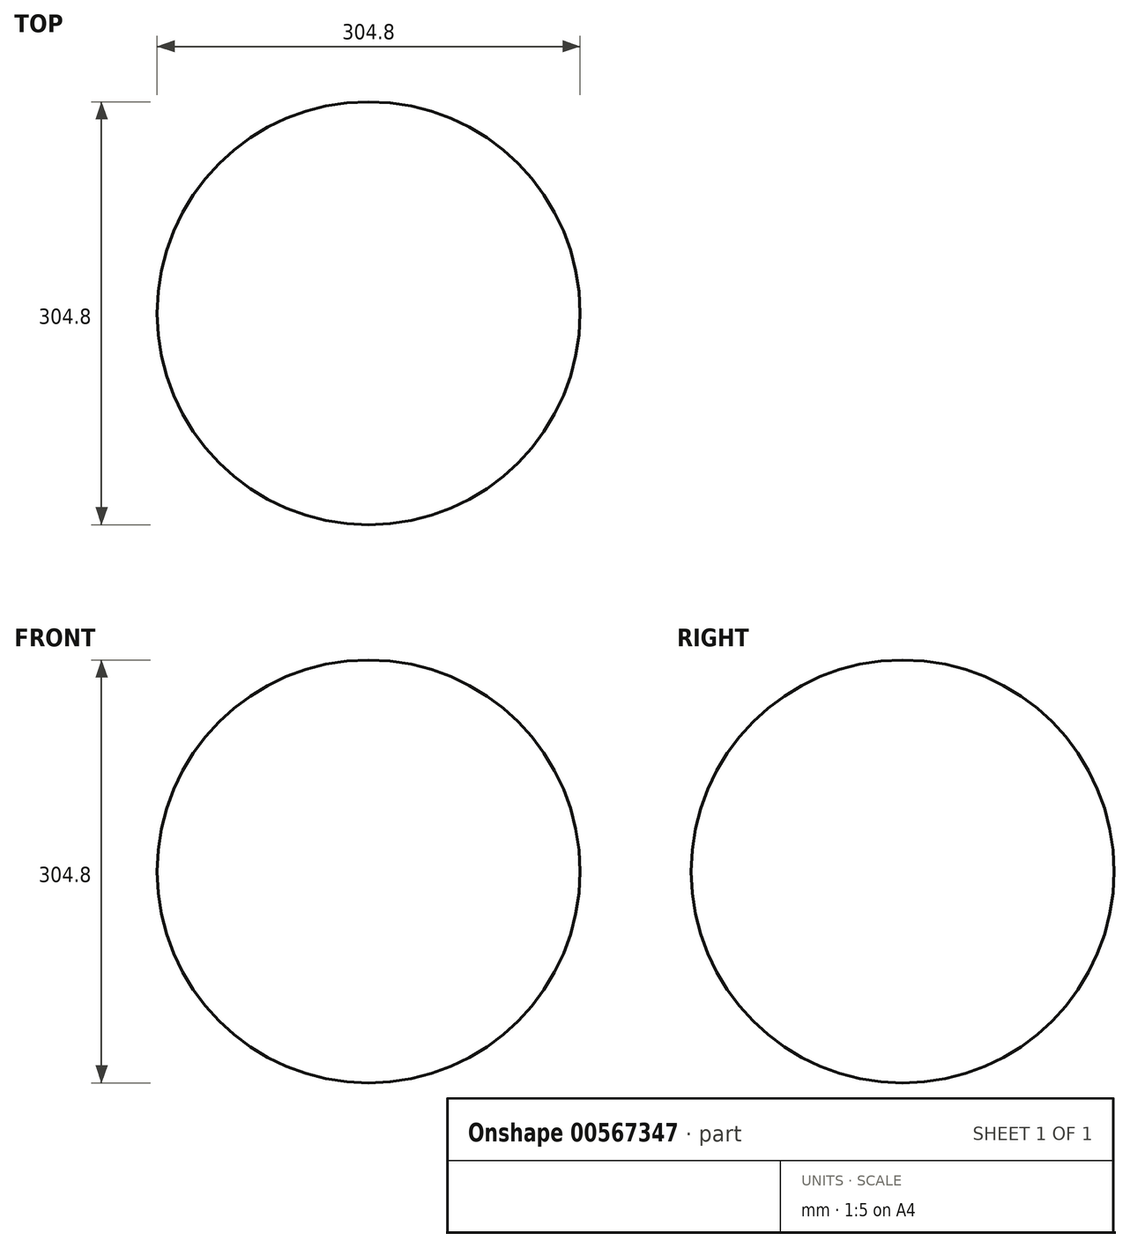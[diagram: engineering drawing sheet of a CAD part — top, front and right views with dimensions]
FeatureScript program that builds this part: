
annotation { "Feature Type Name" : "Feature", "Feature Type Description" : "" }
export const myFeature = defineFeature(function(context is Context, id is Id, definition is map)
    precondition{}
    {
        {
            var Q0;
            Q0=qCreatedBy(makeId("Front.planeOp"),FACE);
            var sketch = newSketch(context, id + "F0", { "sketchPlane" : qUnion([Q0])});
            skArc(sketch, "E0", {"start": v(0, -152.4) * mm, "mid": v(152.4, 0) * mm, "end": v(0, 152.4) * mm});
            skLineSegment(sketch, "E1", {"start": v(0, 0) * mm, "end": v(0, 159.06) * mm});
            skLineSegment(sketch, "E2", {"start": v(0, 0) * mm, "end": v(0, -157.62) * mm});
            skSolve(sketch);
        }
        {
            var Q0;
            {var subQ0=sQuery(id+"F0.wireOp",EDGE,"E0");Q0=makeQuery(id+"F0.imprint","IMPRINT",FACE,{"disambiguationData":[TD([[makeQuery(id+"F0.imprint","IMPRINT",EDGE,{"derivedFrom":subQ0}),1.0]])]});}
            var Q1;
            Q1=sQuery(id+"F0.wireOp",EDGE,"E1");
            revolve(context, id + "F1", {"entities" : qUnion([Q0]), "axis" : qUnion([Q1]), "revolveType" : RevolveType.FULL});
        }
    });
